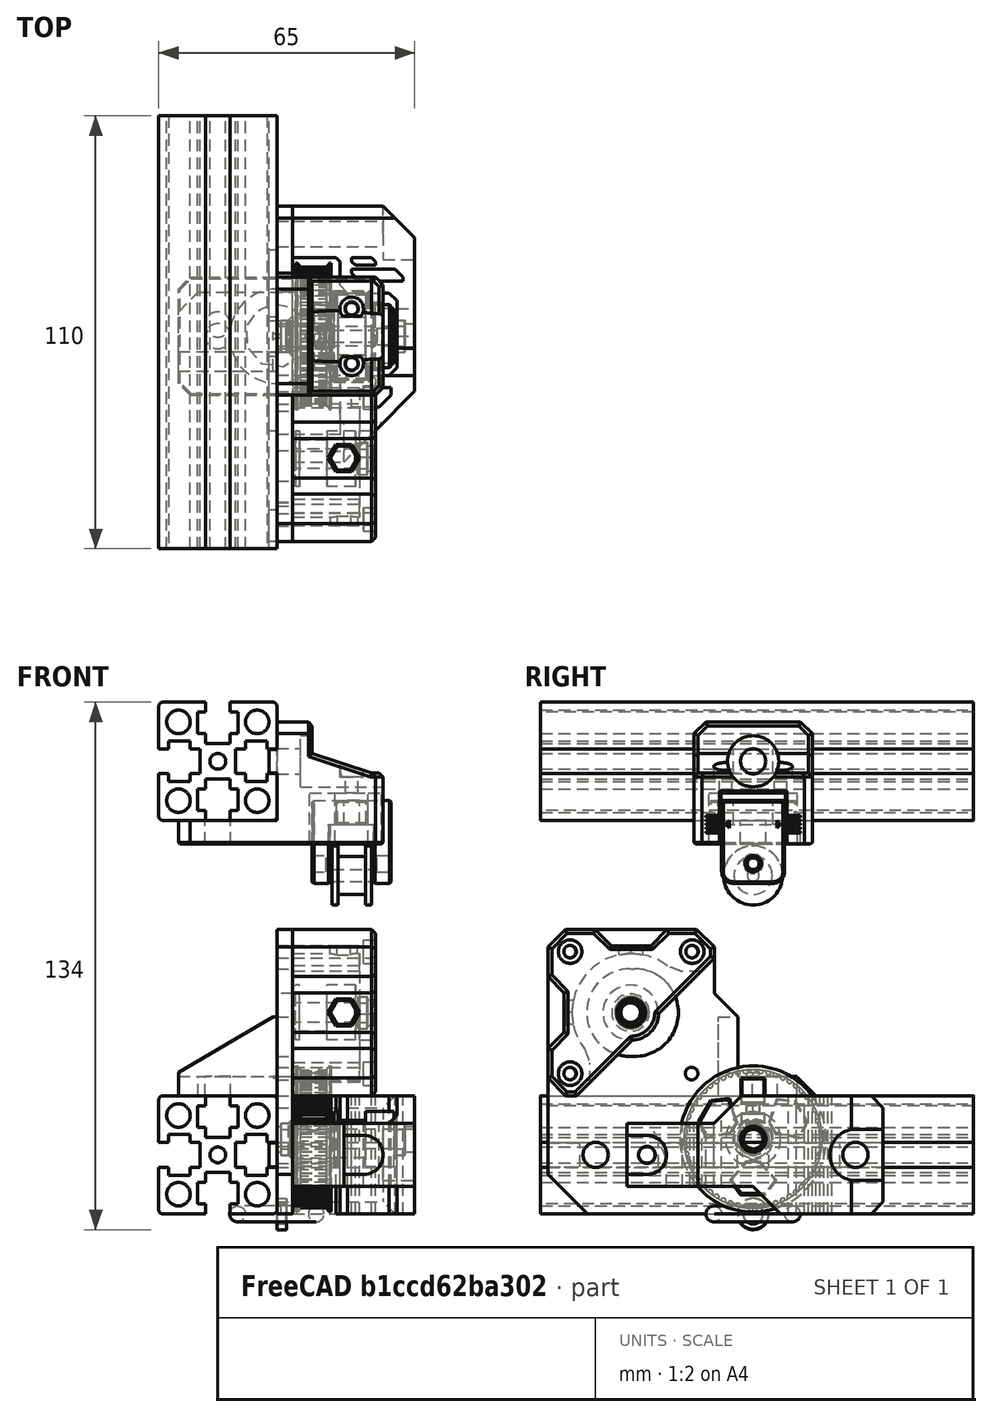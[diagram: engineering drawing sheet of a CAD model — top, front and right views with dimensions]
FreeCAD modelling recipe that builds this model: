
FCSTD DOCUMENT  (FreeCAD 0.18R16146 (Git))
Label: mini-z-belt
License: All rights reserved
LicenseURL: http://en.wikipedia.org/wiki/All_rights_reserved
objects: Part::Box×24, Part::Chamfer×19, Part::Cylinder×19, Part::Feature×17, Part::Cut×16, Part::MultiFuse×15, Mesh::Feature×1, Part::MultiCommon×1, Part::Torus×1
note: 112 computed .brp shape members not serialized (recipe doc carries the construction recipe); baked Part::Feature solids carry a one-line shape summary decoded from their .brp

FEATURE [Part::Feature] Fusion019  label="extrusion-260-001"
  Placement = pos=(-15,-130,15) rot=(-1,0,0;1.5708rad)
  shape: bbox 30 x 260 x 30 mm, 63 faces (baked)
FEATURE [Part::Feature] Part__Feature001  label="56-teeh-gear"
  Placement = pos=(5.9983,-0.0163929,19.0426) rot=(0.707107,0,0.707107;3.14159rad)
  shape: bbox 10.03 x 37.14 x 37.14 mm, 708 faces (baked)
FEATURE [Mesh::Feature] nema17_26mm  label="nema17-26mm"
  Placement = pos=(-26.4,-42,108.8) rot=(0,1,0;1.5708rad)
FEATURE [Part::Feature] Cut002001  label="16-teeth-pulley"
  Placement = pos=(20,-31.15,51.15) rot=(0.707107,0,-0.707107;3.14159rad)
  shape: bbox 15.5 x 14 x 14 mm, 10 faces (baked)
FEATURE [Part::Feature] Cut002002  label="16-teeth-pulley001"
  Placement = pos=(29.7,4e-15,19) rot=(0.707107,0,-0.707107;3.14159rad)
  shape: bbox 15.5 x 14 x 14 mm, 10 faces (baked)
FEATURE [Part::Box] Box  label="Cube"
  AttacherType = Attacher::AttachEngine3D
  Height = 38
  Length = 44
  Placement = pos=(-37,-85,0) rot=(0,0,1;0rad)
  Width = 55
FEATURE [Part::MultiCommon] Common
  Placement = pos=(0,31,0) rot=(0,0,1;0rad)
  Shapes = -> [Box,Fusion019]
FEATURE [Part::Feature] Part__Feature056001001002001005  label="__MR85ZZ-BEARING"
  Placement = pos=(-1e-15,8e-15,-1e-14) rot=(0.57735,-0.57735,0.57735;4.18879rad)
  shape: bbox 2.5 x 8 x 8 mm, 12 faces (baked)
FEATURE [Part::Feature] Part__Feature056001001002001006  label="__MR85ZZ-BEARING001"
  Placement = pos=(1,8e-15,19) rot=(0.57735,-0.57735,0.57735;4.18879rad)
  shape: bbox 2.5 x 8 x 8 mm, 12 faces (baked)
FEATURE [Part::Feature] Part__Feature056001001002001007  label="__MR85ZZ-BEARING002"
  Placement = pos=(30,8e-15,19) rot=(0.57735,-0.57735,0.57735;4.18879rad)
  shape: bbox 2.5 x 8 x 8 mm, 12 faces (baked)
FEATURE [Part::Feature] Common001
  Placement = pos=(0,86,0) rot=(0,0,1;0rad)
  shape: bbox 30 x 55 x 30 mm, 63 faces (baked)
FEATURE [Part::Feature] Part__Feature056001001002001008  label="__MR85ZZ-BEARING003"
  Placement = pos=(20.5,-31.15,51.15) rot=(0.57735,-0.57735,0.57735;4.18879rad)
  shape: bbox 2.5 x 8 x 8 mm, 12 faces (baked)
FEATURE [Part::Box] Box001  label="Cube001"
  AttacherType = Attacher::AttachEngine3D
  Height = 72.3
  Length = 4
  Placement = pos=(0,-52.15,0) rot=(0,0,1;0rad)
  Width = 42.3
FEATURE [Part::Box] Box002  label="Cube002"
  AttacherType = Attacher::AttachEngine3D
  Height = 30
  Length = 4
  Placement = pos=(0,-12,0) rot=(0,0,1;0rad)
  Width = 45
FEATURE [Part::Chamfer] Chamfer
  Base = -> Box001
  Edges = 2 edges r=4.5: [Edge10,Edge12]
FEATURE [Part::Box] Box003  label="Cube003"
  AttacherType = Attacher::AttachEngine3D
  Height = 5
  Length = 29
  Placement = pos=(-25,-9.85,30) rot=(0,0,1;0rad)
  Width = 20
FEATURE [Part::Box] Box004  label="Cube004"
  AttacherType = Attacher::AttachEngine3D
  Height = 20
  Length = 29
  Placement = pos=(-25,-9.85,30) rot=(0,0,1;0rad)
  Width = 6
FEATURE [Part::Cylinder] Cylinder
  Angle = 360
  AttacherType = Attacher::AttachEngine3D
  Height = 10
  Placement = pos=(-1.1e-14,-31.15,51.15) rot=(0,1,0;1.5708rad)
  Radius = 11.15
FEATURE [Part::Cylinder] Cylinder001
  Angle = 360
  AttacherType = Attacher::AttachEngine3D
  Height = 10
  Placement = pos=(-1.4e-14,-46.65,66.65) rot=(0,1,0;1.5708rad)
  Radius = 1.6
FEATURE [Part::Cylinder] Cylinder002
  Angle = 360
  AttacherType = Attacher::AttachEngine3D
  Height = 10
  Placement = pos=(-1.4e-14,-15.65,66.65) rot=(0,1,0;1.5708rad)
  Radius = 1.6
FEATURE [Part::Cylinder] Cylinder003
  Angle = 360
  AttacherType = Attacher::AttachEngine3D
  Height = 10
  Placement = pos=(-8e-15,-46.65,35.65) rot=(0,1,0;1.5708rad)
  Radius = 1.6
FEATURE [Part::Cylinder] Cylinder004
  Angle = 360
  AttacherType = Attacher::AttachEngine3D
  Height = 10
  Placement = pos=(-8e-15,-15.65,35.65) rot=(0,1,0;1.5708rad)
  Radius = 1.6
FEATURE [Part::Cylinder] Cylinder005
  Angle = 360
  AttacherType = Attacher::AttachEngine3D
  Height = 10
  Placement = pos=(-1.1e-14,-30.15,51.15) rot=(0,1,0;1.5708rad)
  Radius = 11.15
FEATURE [Part::MultiFuse] Fusion
  Shapes = -> [Cylinder001,Cylinder003,Cylinder004,Cylinder002]
FEATURE [Part::Box] Box005  label="Cube005"
  AttacherType = Attacher::AttachEngine3D
  Height = 22.3
  Length = 10
  Placement = pos=(0,-31.15,40) rot=(0,0,1;0rad)
  Width = 1
FEATURE [Part::Cylinder] Cylinder006
  Angle = 360
  AttacherType = Attacher::AttachEngine3D
  Height = 10
  Placement = pos=(1,0,19) rot=(0,1,0;1.5708rad)
  Radius = 4.1
FEATURE [Part::Cylinder] Cylinder007
  Angle = 360
  AttacherType = Attacher::AttachEngine3D
  Height = 10
  Placement = pos=(3,0,19) rot=(0,1,0;1.5708rad)
  Radius = 5.1
FEATURE [Part::Chamfer] Chamfer002006002
  Base = -> Cylinder007
  Edges = 1 edges r=1: [Edge3]
FEATURE [Part::MultiFuse] Fusion022
  Shapes = -> [Cylinder006,Chamfer002006002]
FEATURE [Part::Cylinder] Cylinder008
  Angle = 360
  AttacherType = Attacher::AttachEngine3D
  Height = 10
  Placement = pos=(-5,0,19) rot=(0,1,0;1.5708rad)
  Radius = 3.25
FEATURE [Part::Cylinder] Cylinder009
  Angle = 360
  AttacherType = Attacher::AttachEngine3D
  Height = 15
  Placement = pos=(-3e-15,-40,15) rot=(0,1,0;1.5708rad)
  Radius = 3.2
FEATURE [Part::Cylinder] Cylinder010
  Angle = 360
  AttacherType = Attacher::AttachEngine3D
  Height = 15
  Placement = pos=(-3e-15,26,15) rot=(0,1,0;1.5708rad)
  Radius = 3.2
FEATURE [Part::Cylinder] Cylinder013
  Angle = 360
  AttacherType = Attacher::AttachEngine3D
  Height = 42
  Placement = pos=(-3e-15,-27,15) rot=(0,1,0;1.5708rad)
  Radius = 2.15
FEATURE [Part::Chamfer] Chamfer002006006
  Base = -> Box003
  Edges = 1 edges r=5: [Edge3]
FEATURE [Part::Cylinder] Cylinder014
  Angle = 360
  AttacherType = Attacher::AttachEngine3D
  Height = 10
  Placement = pos=(-15,2,27) rot=(0,0,1;0rad)
  Radius = 3.2
FEATURE [Part::Cut] Cut002007
  Base = -> Chamfer002006006
  Placement = pos=(0,1,0) rot=(0,0,1;0rad)
  Tool = -> Cylinder014
FEATURE [Part::Cylinder] Cylinder015
  Angle = 360
  AttacherType = Attacher::AttachEngine3D
  Height = 15
  Placement = pos=(-3e-15,-27,15) rot=(0,1,0;1.5708rad)
  Radius = 2.1
FEATURE [Part::Chamfer] Chamfer002006010
  Base = -> Box002
  Edges = 2 edges r=3: [Edge11,Edge12]
FEATURE [Part::Cut] Cut002008
  Base = -> Chamfer002006010
  Tool = -> Fusion022
FEATURE [Part::Cut] Cut002009
  Base = -> Cut002008
  Tool = -> Cylinder008
FEATURE [Part::Cut] Cut002010
  Base = -> Cut002009
  Tool = -> Cylinder010
FEATURE [Part::Box] Box006  label="Cube006"
  AttacherType = Attacher::AttachEngine3D
  Height = 30
  Length = 12
  Placement = pos=(4,-22,0) rot=(0,0,1;0rad)
  Width = 42
FEATURE [Part::Box] Box007  label="Cube007"
  AttacherType = Attacher::AttachEngine3D
  Height = 30
  Length = 31
  Placement = pos=(4,-32,0) rot=(0,0,1;0rad)
  Width = 65
FEATURE [Part::Box] Box008  label="Cube008"
  AttacherType = Attacher::AttachEngine3D
  Height = 30
  Length = 14.5
  Placement = pos=(16,-10,0) rot=(0,0,1;0rad)
  Width = 21
FEATURE [Part::Feature] Box006001  label="Cube009"
  Placement = pos=(0,0,19) rot=(1,0,0;0.436332rad)
  shape: bbox 12 x 52.56 x 45.78 mm, 6 faces (baked)
FEATURE [Part::Box] Box006003  label="Cube011"
  AttacherType = Attacher::AttachEngine3D
  Height = 15
  Length = 36
  Placement = pos=(4,-47,20) rot=(0,0,1;0rad)
  Width = 42
FEATURE [Part::Box] Box006004  label="Cube012"
  AttacherType = Attacher::AttachEngine3D
  Height = 15
  Length = 36
  Placement = pos=(4,-32,-5) rot=(0,0,1;0rad)
  Width = 42
FEATURE [Part::Chamfer] Chamfer002006013
  Base = -> Box006004
  Edges = 1 edges r=10: [Edge12]
  Placement = pos=(0,0,-3) rot=(0,0,1;0rad)
FEATURE [Part::Chamfer] Chamfer002006014
  Base = -> Box006003
  Edges = 1 edges r=10: [Edge11]
  Placement = pos=(0,5,3) rot=(0,0,1;0rad)
FEATURE [Part::Box] Box006005  label="Cube013"
  AttacherType = Attacher::AttachEngine3D
  Height = 27
  Length = 21
  Placement = pos=(19,-33,0) rot=(0,0,1;0rad)
  Width = 22
FEATURE [Part::Chamfer] Chamfer002006015
  Base = -> Box006005
  Edges = 1 edges r=19: [Edge3]
  Placement = pos=(-2,-2,0) rot=(0,0,1;0rad)
FEATURE [Part::Box] Box006006  label="Cube014"
  AttacherType = Attacher::AttachEngine3D
  Height = 31
  Length = 30
  Placement = pos=(38,24,0) rot=(0,0,1;0rad)
  Width = 30
FEATURE [Part::Chamfer] Chamfer002006016
  Base = -> Box006006
  Edges = 1 edges r=20: [Edge1]
  Placement = pos=(-12,-10,0) rot=(0,0,1;0rad)
FEATURE [Part::Cylinder] Cylinder018
  Angle = 360
  AttacherType = Attacher::AttachEngine3D
  Height = 39
  Placement = pos=(28,26,15) rot=(0,1,0;1.5708rad)
  Radius = 6.5
FEATURE [Part::Box] Box006007  label="Cube015"
  AttacherType = Attacher::AttachEngine3D
  Height = 13
  Length = 39
  Placement = pos=(28,26,8.5) rot=(0,0,1;0rad)
  Width = 17
FEATURE [Part::Cylinder] Cylinder021
  Angle = 360
  AttacherType = Attacher::AttachEngine3D
  Height = 42
  Placement = pos=(17,-27,15) rot=(0,1,0;1.5708rad)
  Radius = 5
FEATURE [Part::Box] Box006009  label="Cube017"
  AttacherType = Attacher::AttachEngine3D
  Height = 31
  Length = 13
  Placement = pos=(19,14,0) rot=(0,0,1;0rad)
  Width = 3
FEATURE [Part::Cylinder] Cylinder022
  Angle = 360
  AttacherType = Attacher::AttachEngine3D
  Height = 3
  Placement = pos=(29.5,0,19) rot=(0,1,0;1.5708rad)
  Radius = 4.1
FEATURE [Part::Cylinder] Cylinder023
  Angle = 360
  AttacherType = Attacher::AttachEngine3D
  Height = 11
  Placement = pos=(31,0,19) rot=(0,1,0;1.5708rad)
  Radius = 3.25
FEATURE [Part::MultiFuse] Fusion029
  Shapes = -> [Cylinder022,Cylinder023]
FEATURE [Part::Box] Box006010  label="Cube018"
  AttacherType = Attacher::AttachEngine3D
  Height = 20
  Length = 29
  Placement = pos=(-29,-14.85,30) rot=(0,0,1;0rad)
  Width = 6
FEATURE [Part::Cut] Cut002023
  Base = -> Box004
  Tool = -> Box006010
FEATURE [Part::MultiFuse] Fusion030
  Shapes = -> [Box005,Cylinder005,Cylinder]
FEATURE [Part::MultiFuse] Fusion031
  Shapes = -> [Fusion030,Fusion]
FEATURE [Part::Cut] Cut
  Base = -> Chamfer
  Tool = -> Fusion031
FEATURE [Part::Chamfer] Chamfer002006025
  Base = -> Cut002023
  Edges = 1 edges: [Edge1 r1=14 r2=24]
FEATURE [Part::Chamfer] Chamfer002006026
  Base = -> Cut
  Edges = 1 edges r=10: [Edge17]
FEATURE [Part::MultiFuse] Fusion032
  Shapes = -> [Chamfer002006026,Chamfer002006025,Cut002007]
FEATURE [Part::Box] Box006011  label="Cube019"
  AttacherType = Attacher::AttachEngine3D
  Height = 7.15
  Length = 4
  Placement = pos=(0,-11,49) rot=(0,0,1;0rad)
  Width = 7.15
FEATURE [Part::Box] Box006013  label="Cube021"
  AttacherType = Attacher::AttachEngine3D
  Height = 6
  Length = 4
  Placement = pos=(0,10,29) rot=(0,0,1;0rad)
  Width = 6
FEATURE [Part::Chamfer] Chamfer002006027
  Base = -> Box006011
  Edges = 1 edges r=6.15: [Edge12]
FEATURE [Part::Chamfer] Chamfer002006028
  Base = -> Box006013
  Edges = 1 edges r=5: [Edge12]
FEATURE [Part::MultiFuse] Fusion033
  Shapes = -> [Fusion032,Chamfer002006027,Chamfer002006028,Cut002010]
FEATURE [Part::Cut] Cut002024
  Base = -> Fusion033
  Tool = -> Cylinder009
FEATURE [Part::Cylinder] Cylinder024
  Angle = 360
  AttacherType = Attacher::AttachEngine3D
  Height = 40
  Placement = pos=(-3e-15,26,15) rot=(0,1,0;1.5708rad)
  Radius = 3.2
FEATURE [Part::MultiFuse] Fusion034
  Placement = pos=(-1,0,0) rot=(0,0,1;0rad)
  Shapes = -> [Cylinder018,Box006007]
FEATURE [Part::Box] Box006014  label="Cube022"
  AttacherType = Attacher::AttachEngine3D
  Height = 30
  Length = 10
  Placement = pos=(19,-18,0) rot=(0,0,1;0rad)
  Width = 5
FEATURE [Part::Box] Box006015  label="Cube023"
  AttacherType = Attacher::AttachEngine3D
  Height = 31
  Length = 6
  Placement = pos=(19,18,0) rot=(0,0,1;0rad)
  Width = 2
FEATURE [Part::Chamfer] Chamfer002006034
  Base = -> Box006009
  Edges = 1 edges r=2: [Edge1]
FEATURE [Part::Chamfer] Chamfer002006035
  Base = -> Chamfer002006034
  Edges = 1 edges r=2: [Edge12]
FEATURE [Part::Chamfer] Chamfer002006036
  Base = -> Box006015
  Edges = 2 edges r=1: [Edge1,Edge7]
FEATURE [Part::MultiFuse] Fusion038
  Shapes = -> [Box008,Box006001,Box006]
FEATURE [Part::Cut] Cut002026
  Base = -> Box007
  Tool = -> Fusion038
FEATURE [Part::Chamfer] Chamfer002006037
  Base = -> Cut002026
  Edges = 2 edges r=3: [Edge16,Edge30]
FEATURE [Part::Chamfer] Chamfer002006038
  Base = -> Chamfer002006037
  Edges = 4 edges r=2: [Edge34,Edge39,Edge42,Edge47]
FEATURE [Part::Chamfer] Chamfer002006039
  Base = -> Chamfer002006038
  Edges = 1 edges r=1: [Edge26]
FEATURE [Part::Feature] Body001  label="_center-mark-515"
  shape: bbox 1 x 2 x 2 mm, 5 faces (baked)
FEATURE [Part::Feature] Body002  label="_center-mark001"
  Placement = pos=(-1,0,34.5) rot=(0,0,1;0rad)
  shape: bbox 1 x 2 x 2 mm, 5 faces (baked)
FEATURE [Part::Box] Box006016  label="Cube024"
  AttacherType = Attacher::AttachEngine3D
  Height = 6
  Length = 2
  Placement = pos=(-2,-52,12) rot=(0,0,1;0rad)
  Width = 8
FEATURE [Part::Box] Box006017  label="Cube025"
  AttacherType = Attacher::AttachEngine3D
  Height = 6
  Length = 2
  Placement = pos=(-2,-24,12) rot=(0,0,1;0rad)
  Width = 20
FEATURE [Part::Box] Box006018  label="Cube026"
  AttacherType = Attacher::AttachEngine3D
  Height = 6
  Length = 2
  Placement = pos=(-2,4,12) rot=(0,0,1;0rad)
  Width = 18
FEATURE [Part::MultiFuse] Fusion040  label="aligner"
  Shapes = -> [Box006018,Box006017,Box006016]
FEATURE [Part::Feature] Cut001  label="_16-teeth-idler"
  Placement = pos=(14,0,86) rot=(0,1,0;1.5708rad)
  shape: bbox 10 x 15 x 15 mm, 8 faces (baked)
FEATURE [Part::MultiFuse] Fusion041004  label="_3030-extrusion-001"
  Shapes = -> [Common001,Common]
FEATURE [Part::Feature] Fusion041004001  label="_3030-extrusion-002"
  Placement = pos=(0,0,100) rot=(0,0,1;0rad)
  shape: bbox 30 x 110 x 30 mm, 124 faces (baked)
FEATURE [Part::MultiFuse] Fusion041004010002
  Shapes = -> [Cylinder013,Cylinder021]
FEATURE [Part::Box] Box006019  label="Cube027"
  AttacherType = Attacher::AttachEngine3D
  Height = 10
  Length = 42
  Placement = pos=(17,-32,10) rot=(0,0,1;0rad)
  Width = 5
FEATURE [Part::MultiFuse] Fusion041004010003
  Shapes = -> [Cylinder024,Fusion034,Fusion029,Fusion041004010002,Box006019]
FEATURE [Part::Cut] Cut002034
  Base = -> Chamfer002006039
  Tool = -> Fusion041004010003
FEATURE [Part::Cut] Cut002035
  Base = -> Cut002034
  Tool = -> Chamfer002006014
FEATURE [Part::Cut] Cut002036
  Base = -> Cut002035
  Tool = -> Chamfer002006013
FEATURE [Part::Chamfer] Chamfer002006040
  Base = -> Box006014
  Edges = 2 edges r=3: [Edge3,Edge5]
FEATURE [Part::Cut] Cut002037
  Base = -> Cut002036
  Tool = -> Chamfer002006015
FEATURE [Part::MultiFuse] Fusion041004010004
  Shapes = -> [Chamfer002006040,Chamfer002006035,Chamfer002006036]
FEATURE [Part::Cut] Cut002038
  Base = -> Cut002037
  Tool = -> Fusion041004010004
FEATURE [Part::Cut] Cut002039
  Base = -> Cut002038
  Tool = -> Chamfer002006016
FEATURE [Part::Feature] Cut002003001  label="Cut002004"
  Placement = pos=(4,-31,51.15) rot=(0,1,0;1.5708rad)
  shape: bbox 21.52 x 42.3 x 42.3 mm, 81 faces (baked)
FEATURE [Part::Feature] Cut009010005001  label="Cut009010007"
  Placement = pos=(19,0,100) rot=(0,0,1;0rad)
  shape: bbox 20 x 22 x 21 mm, 102 faces (baked)
FEATURE [Part::Feature] Cut009010004001  label="Cut009010006"
  Placement = pos=(19,0,100) rot=(0,0,1;0rad)
  shape: bbox 52 x 30 x 31 mm, 124 faces (baked)
FEATURE [Part::Cut] Cut009010005002
  Base = -> Cut002024
  Tool = -> Cylinder015
FEATURE [Part::Cut] Cut009010005003
  Base = -> Cut009010005002
  Tool = -> Body002
FEATURE [Part::MultiFuse] Fusion041004010005
  Shapes = -> [Fusion040,Cut009010005003]
FEATURE [Part::Torus] Torus  label="82teeth-belt"
  Angle1 = -180
  Angle2 = 180
  Angle3 = 360
  AttacherType = Attacher::AttachEngine3D
  Radius1 = 10
  Radius2 = 2
